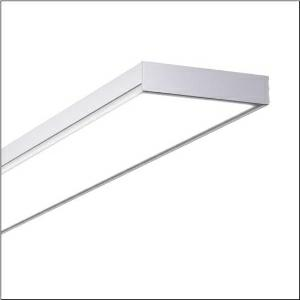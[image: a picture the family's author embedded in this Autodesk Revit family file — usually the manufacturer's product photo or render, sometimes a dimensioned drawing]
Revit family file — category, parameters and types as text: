
# Revit family: apollon_r__31_51mp26wd2441e_4be8
name_source: partatom
category: Lighting Fixtures
units: mm (PartAtom-declared; Revit-internal decimal feet)

## family parameters
Cut with Voids When Loaded = No
Host = Face
Light Source = No
Part Type = Normal
Room Calculation Point = No
Round Connector Dimension = Use Diameter
Shared = No

## types (1)
- Apollon® 31 (1 x LED, 4600 lm, 33 W, 4000K)
    Apparent Load = 33 VA
    CIE Flux Codes = 61 87 97 97 100
    Color Rendering = 80
    Color Temperature = 4000K
    Default Elevation = 1800 mm
    Description = Apollon® 31, office luminaire, primary optical cover: micro prismatic cover, of PMMA, light emission: direct distribution, primary light characteristic: symmetric, installation type: surface-mounted, LED, rated luminous flux: 4.600lm, luminous efficacy: 139lm/W, light colour: 840, colour temperature: 4000K, control gear: ECG DALI, with terminal, 5-pole, mains connection: 220..240V, AC, 50/60Hz, rated input power: 33W, housing, of sheet steel, coil coated, metallic grey (RAL 9006), length: 1.545mm, width: 200mm, height: 44mm, protection rating (complete): IP20, insulation class (complete): insulation class II (safety insulation), certification: CE, impact resistance: IK02, permissible operating ambient temperature: -20..+40°C, standard: EN 60598-2-22, packaging unit: 1 piece
    Height = 44 mm
    Lamp = 1 x LED
    Lamp Light Flux = 4600 lm
    Lamp Power = 33 W
    Lamp count = 1
    Length = 1545 mm
    Luminous efficacy = 139 lm/W
    Manufacturer = Siteco
    ModVariant = No
    Model = 51MP26WD2441E
    Mounting Place = Ceiling
    Mounting Type = Surface mounted
    Number of Poles = 1
    OnlyDefault = Yes
    Power Factor = 1
    Product Name = Apollon® 31
    Product group = office luminaire | ceiling mounted
    ProductGroupID = 302
    Protection Class = Protection class II
    Protection Degree = IP 20
    RLX_Detail_Level = 1
    RlxData = <blob elided: 24105 chars, md5=6b2e685a>
    Socket = socket
    Standby Power = 0 W
    System Light Flux = 4600 lm
    System Power = 33 W
    Type Comments = Product without accessories
    Type Image = l_1007091.jpg
    URL = http://relux.com
    VarID = ---
    Voltage = 0 V
    Weight = 0.00 kg
    Width = 200 mm  [stored 0.656168 ft]

note: [stored X ft] marks values corroborated as IEEE doubles in the binary element streams (Revit-internal decimal feet)

## geometry (parser evidence)
native form markers: Blend x4, Sweep x9
no freeform markers — native parametric forms only
